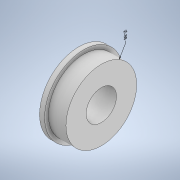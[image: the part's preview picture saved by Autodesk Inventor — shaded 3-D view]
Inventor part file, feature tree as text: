
AUTODESK INVENTOR PART (.ipt)
format: ipt  version: 2020.2 (Build 242310000, 310)  size: 131,584 bytes
history: native  units: in
note: dims shown in document units (in); Inventor stores cm internally (conversion verified against a paired STEP export)
features: other x2, revolve x1
ambient origin geometry x8: Origin, YZ Plane, XZ Plane, XY Plane, X Axis, Y Axis, Z Axis, Center Point
bodies: Solid1 (feature_tree)
feature tree (3):
  other  "Annotations"
  revolve  "Revolve1"  [1 undecoded]
  other  "Diameter Dimension 1"
note: 1 required parameter value undecoded (feature->parameter linkage not recoverable at this tier; creation-order binding heuristic only, values carry confidence <= 0.55)
